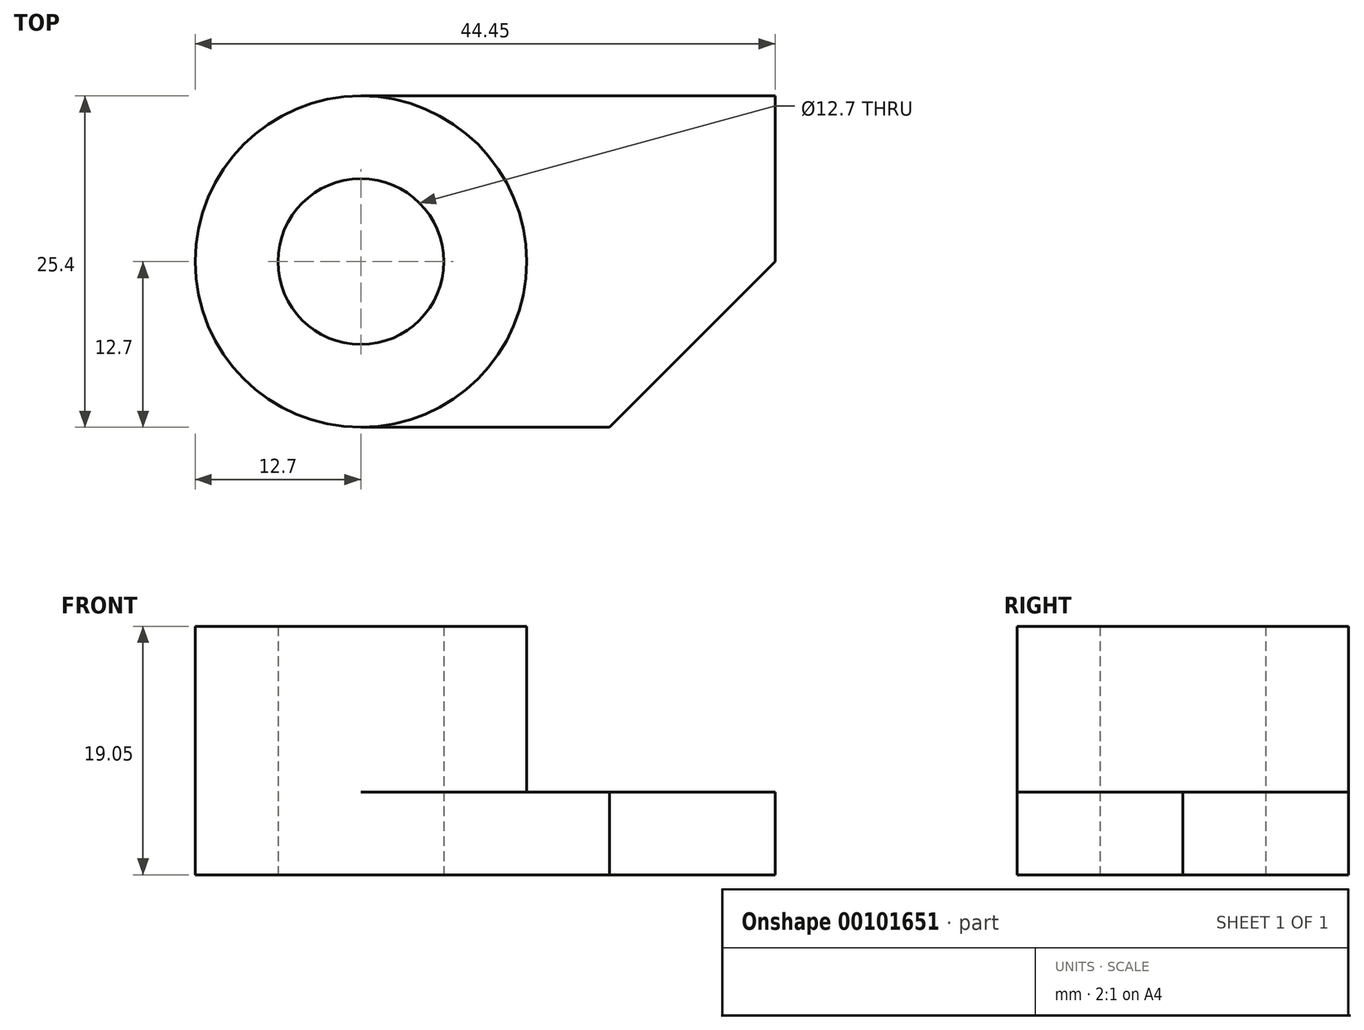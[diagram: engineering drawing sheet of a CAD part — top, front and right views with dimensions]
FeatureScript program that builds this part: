
annotation { "Feature Type Name" : "Feature", "Feature Type Description" : "" }
export const myFeature = defineFeature(function(context is Context, id is Id, definition is map)
    precondition{}
    {
        {
            var Q0;
            Q0=qCreatedBy(makeId("Top.planeOp"),FACE);
            var sketch = newSketch(context, id + "F0", { "sketchPlane" : qUnion([Q0])});
            skLineSegment(sketch, "E0", {"start": v(0, 0) * mm, "end": v(-31.75, 0) * mm});
            skLineSegment(sketch, "E1", {"start": v(0, 0) * mm, "end": v(0, -12.7) * mm});
            skLineSegment(sketch, "E2", {"start": v(0, -12.7) * mm, "end": v(-12.7, -25.4) * mm});
            skLineSegment(sketch, "E3", {"start": v(-12.7, -25.4) * mm, "end": v(-31.75, -25.4) * mm});
            skCircle(sketch, "E4", {"center": v(-31.75, -12.7) * mm, "radius": 6.35 * mm});
            skCircle(sketch, "E5", {"center": v(-31.75, -12.7) * mm, "radius": 12.7 * mm});
            skSolve(sketch);
        }
        {
            var Q0;
            Q0=makeQuery(id+"F0.imprint","IMPRINT",FACE,{"disambiguationData":[TD([[makeQuery(id+"F0.imprint","IMPRINT",EDGE,{"derivedFrom":sQuery(id+"F0.wireOp",EDGE,"E4")}),-1.0]])]});
            var Q1;
            Q1=sQuery(id+"F0.wireOp",EDGE,"E5");
            var Q2;
            Q2=sQuery(id+"F0.wireOp",EDGE,"E4");
            extrude(context, id + "F1", {"entities" : qUnion([Q0]), "surfaceEntities" : qUnion([Q1, Q2]), "depth" : 19.05 * mm});
        }
        {
            var Q0;
            {var subQ1=sQuery(id+"F0.wireOp",EDGE,"E0");Q0=makeQuery(id+"F0.imprint","IMPRINT",FACE,{"disambiguationData":[TD([[makeQuery(id+"F0.imprint","IMPRINT",EDGE,{"derivedFrom":subQ1}),1.0]])]});}
            extrude(context, id + "F2", {"entities" : qUnion([Q0]), "operationType" : NewBodyOperationType.ADD, "depth" : 6.35 * mm});
        }
    });
